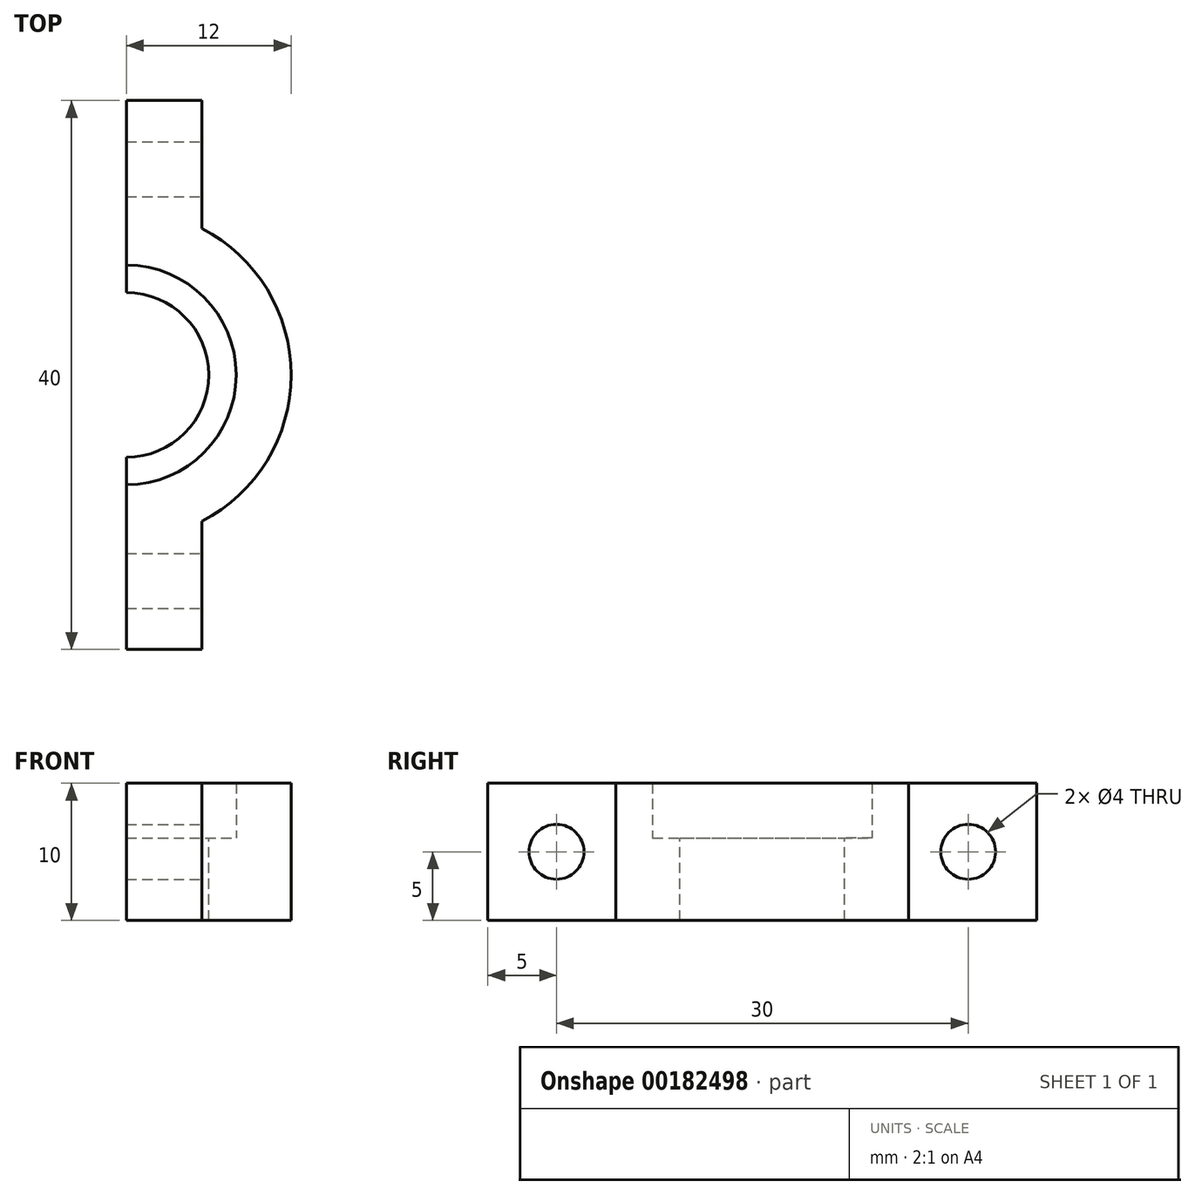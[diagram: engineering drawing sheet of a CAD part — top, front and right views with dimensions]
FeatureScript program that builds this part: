
annotation { "Feature Type Name" : "Feature", "Feature Type Description" : "" }
export const myFeature = defineFeature(function(context is Context, id is Id, definition is map)
    precondition{}
    {
        {
            var Q0;
            Q0=qCreatedBy(makeId("Top.planeOp"),FACE);
            var sketch = newSketch(context, id + "F0", { "sketchPlane" : qUnion([Q0])});
            skCircle(sketch, "E0.cCircle", {"center": v(0, 0) * mm, "radius": 46.19 * mm, "construction": true});
            skLineSegment(sketch, "E0.0", {"start": v(-80, 46.19) * mm, "end": v(80, 46.19) * mm, "construction": true});
            skLineSegment(sketch, "E0.1", {"start": v(80, 46.19) * mm, "end": v(0, -92.38) * mm, "construction": true});
            skLineSegment(sketch, "E0.2", {"start": v(0, -92.38) * mm, "end": v(-80, 46.19) * mm, "construction": true});
            skPoint(sketch, "E0.0.midPoint", {"position": v(0, 46.19) * mm});
            skLineSegment(sketch, "E1", {"start": v(40, 46.19) * mm, "end": v(60, 11.55) * mm});
            skLineSegment(sketch, "E2", {"start": v(-40, 46.19) * mm, "end": v(-60, 11.55) * mm});
            skLineSegment(sketch, "E3", {"start": v(-20, -57.74) * mm, "end": v(20, -57.74) * mm});
            skLineSegment(sketch, "E4", {"start": v(-40, 46.19) * mm, "end": v(40, 46.19) * mm});
            skLineSegment(sketch, "E5", {"start": v(60, 11.55) * mm, "end": v(20, -57.74) * mm});
            skLineSegment(sketch, "E6", {"start": v(-20, -57.74) * mm, "end": v(-60, 11.55) * mm});
            skSolve(sketch);
        }
        {
            var Q0;
            Q0=makeQuery(id+"F0.imprint","IMPRINT",FACE,{"disambiguationData":[TD([[makeQuery(id+"F0.imprint","IMPRINT",EDGE,{"derivedFrom":sQuery(id+"F0.wireOp",EDGE,"E1")}),-1.0]])]});
            extrude(context, id + "F1", {"entities" : qUnion([Q0]), "depth" : 10 * mm});
        }
        {
            var Q0;
            Q0=makeQuery(id+"F1.opExtrude","CAP_FACE",FACE,{"disambiguationData":[OSD([sQuery(id+"F0.wireOp",EDGE,"E1"),sQuery(id+"F0.wireOp",EDGE,"E2"),sQuery(id+"F0.wireOp",EDGE,"E3"),sQuery(id+"F0.wireOp",EDGE,"E4"),sQuery(id+"F0.wireOp",EDGE,"E5"),sQuery(id+"F0.wireOp",EDGE,"E6")])],"isStart":false});
            var sketch = newSketch(context, id + "F2", { "sketchPlane" : qUnion([Q0])});
            skLineSegment(sketch, "E7.0", {"start": v(-48.45, 21.55) * mm, "end": v(-5.57, -52.74) * mm});
            skLineSegment(sketch, "E7.1", {"start": v(5.57, -52.74) * mm, "end": v(48.45, 21.55) * mm});
            skLineSegment(sketch, "E7.2", {"start": v(48.45, 21.55) * mm, "end": v(42.89, 31.19) * mm});
            skLineSegment(sketch, "E7.3", {"start": v(-5.57, -52.74) * mm, "end": v(5.57, -52.74) * mm});
            skLineSegment(sketch, "E7.4", {"start": v(42.89, 31.19) * mm, "end": v(-42.89, 31.19) * mm});
            skLineSegment(sketch, "E7.5", {"start": v(-42.89, 31.19) * mm, "end": v(-48.45, 21.55) * mm});
            skSolve(sketch);
        }
        {
            var Q0;
            Q0=makeQuery(id+"F2.imprint","IMPRINT",FACE,{"disambiguationData":[TD([[makeQuery(id+"F2.imprint","IMPRINT",EDGE,{"derivedFrom":sQuery(id+"F2.wireOp",EDGE,"E7.0")}),1.0]])]});
            extrude(context, id + "F3", {"entities" : qUnion([Q0]), "operationType" : NewBodyOperationType.REMOVE, "oppositeDirection" : true, "depth" : 4 * mm});
        }
        {
            var Q0;
            Q0=makeQuery(id+"F3.boolean.opBoolean","COPY",FACE,{"derivedFrom":makeQuery(id+"F3.opExtrude","CAP_FACE",FACE,{"disambiguationData":[OSD([sQuery(id+"F2.wireOp",EDGE,"E7.0"),sQuery(id+"F2.wireOp",EDGE,"E7.1"),sQuery(id+"F2.wireOp",EDGE,"E7.2"),sQuery(id+"F2.wireOp",EDGE,"E7.3"),sQuery(id+"F2.wireOp",EDGE,"E7.4"),sQuery(id+"F2.wireOp",EDGE,"E7.5")])],"isStart":false})});
            var sketch = newSketch(context, id + "F4", { "sketchPlane" : qUnion([Q0])});
            skCircle(sketch, "E8", {"center": v(0, 0) * mm, "radius": 6 * mm});
            skLineSegment(sketch, "E9", {"start": v(0, 31.19) * mm, "end": v(0, 6) * mm});
            skLineSegment(sketch, "E10", {"start": v(0, -52.74) * mm, "end": v(0, -6) * mm});
            skLineSegment(sketch, "E11", {"start": v(5.5, 31.19) * mm, "end": v(5.5, -52.74) * mm});
            skLineSegment(sketch, "E12", {"start": v(0, 20) * mm, "end": v(5.5, 20) * mm});
            skLineSegment(sketch, "E13", {"start": v(0, -20) * mm, "end": v(5.5, -20) * mm});
            skLineSegment(sketch, "E14.0", {"start": v(-5.5, 31.19) * mm, "end": v(-5.5, -52.74) * mm});
            skCircle(sketch, "E15", {"center": v(0, 0) * mm, "radius": 8 * mm});
            skCircle(sketch, "E16", {"center": v(0, 0) * mm, "radius": 12 * mm});
            skLineSegment(sketch, "E17", {"start": v(-11.35, -42.72) * mm, "end": v(11.35, -42.72) * mm});
            skLineSegment(sketch, "E18", {"start": v(0, 20) * mm, "end": v(-5.5, 20) * mm});
            skLineSegment(sketch, "E19", {"start": v(0, -20) * mm, "end": v(-5.5, -20) * mm});
            skSolve(sketch);
        }
        {
            var Q0;
            {var subQ10=makeQuery(id+"F3.boolean.opBoolean","COPY",EDGE,{"derivedFrom":makeQuery(id+"F3.opExtrude","CAP_EDGE",EDGE,{"disambiguationData":[OSD([sQuery(id+"F2.wireOp",EDGE,"E7.5")])],"isStart":false})});Q0=makeQuery(id+"F4.imprint","IMPRINT",FACE,{"disambiguationData":[TD([[makeQuery(id+"F4.imprint","IMPRINT",EDGE,{"derivedFrom":subQ10}),1.0]])]});}
            var Q1;
            {var subQ3=sQuery(id+"F4.wireOp",EDGE,"E12");Q1=makeQuery(id+"F4.imprint","IMPRINT",FACE,{"disambiguationData":[TD([[makeQuery(id+"F4.imprint","IMPRINT",EDGE,{"derivedFrom":subQ3}),1.0]])]});}
            var Q2;
            {var subQ3=sQuery(id+"F4.wireOp",EDGE,"E18");Q2=makeQuery(id+"F4.imprint","IMPRINT",FACE,{"disambiguationData":[TD([[makeQuery(id+"F4.imprint","IMPRINT",EDGE,{"derivedFrom":subQ3}),-1.0]])]});}
            var Q3;
            {var subQ0=sQuery(id+"F4.wireOp",EDGE,"E18");Q3=makeQuery(id+"F4.imprint","IMPRINT",FACE,{"disambiguationData":[TD([[makeQuery(id+"F4.imprint","IMPRINT",EDGE,{"derivedFrom":subQ0}),1.0]])]});}
            var Q4;
            {var subQ0=sQuery(id+"F4.wireOp",EDGE,"E16");var subQ1=sQuery(id+"F4.wireOp",EDGE,"E9");var subQ2=makeQuery(id+"F4.imprint","INTERSECT",VERTEX,{"derivedFrom":[subQ1,subQ0]});Q4=makeQuery(id+"F4.imprint","IMPRINT",FACE,{"disambiguationData":[TD([[makeQuery(id+"F4.imprint","IMPRINT",EDGE,{"disambiguationData":[TD([[subQ2,-1.0]])],"derivedFrom":subQ1}),-1.0]])]});}
            var Q5;
            {var subQ0=sQuery(id+"F4.wireOp",EDGE,"E9");var subQ1=sQuery(id+"F4.wireOp",EDGE,"E8");var subQ2=makeQuery(id+"F4.imprint","INTERSECT",VERTEX,{"derivedFrom":[subQ1,subQ0]});Q5=makeQuery(id+"F4.imprint","IMPRINT",FACE,{"disambiguationData":[TD([[makeQuery(id+"F4.imprint","IMPRINT",EDGE,{"disambiguationData":[TD([[subQ2,-1.0]])],"derivedFrom":subQ1}),-1.0]])]});}
            var Q6;
            {var subQ0=sQuery(id+"F4.wireOp",EDGE,"E8");var subQ4=makeQuery(id+"F4.imprint","INTERSECT",VERTEX,{"derivedFrom":[subQ0,sQuery(id+"F4.wireOp",EDGE,"E9")]});Q6=makeQuery(id+"F4.imprint","IMPRINT",FACE,{"disambiguationData":[TD([[makeQuery(id+"F4.imprint","IMPRINT",EDGE,{"disambiguationData":[TD([[subQ4,1.0]])],"derivedFrom":subQ0}),1.0]])]});}
            var Q7;
            {var subQ0=sQuery(id+"F4.wireOp",EDGE,"E14.0");var subQ1=sQuery(id+"F4.wireOp",EDGE,"E8");var subQ2=makeQuery(id+"F4.imprint","INTERSECT",VERTEX,{"disambiguationData":[OD(0.0)],"derivedFrom":[subQ1,subQ0]});Q7=makeQuery(id+"F4.imprint","IMPRINT",FACE,{"disambiguationData":[TD([[makeQuery(id+"F4.imprint","IMPRINT",EDGE,{"disambiguationData":[TD([[subQ2,-1.0]])],"derivedFrom":subQ1}),-1.0]])]});}
            var Q8;
            {var subQ0=sQuery(id+"F4.wireOp",EDGE,"E16");var subQ1=sQuery(id+"F4.wireOp",EDGE,"E14.0");var subQ2=makeQuery(id+"F4.imprint","INTERSECT",VERTEX,{"disambiguationData":[OD(0.0)],"derivedFrom":[subQ1,subQ0]});Q8=makeQuery(id+"F4.imprint","IMPRINT",FACE,{"disambiguationData":[TD([[makeQuery(id+"F4.imprint","IMPRINT",EDGE,{"disambiguationData":[TD([[subQ2,-1.0]])],"derivedFrom":subQ1}),-1.0]])]});}
            var Q9;
            {var subQ0=sQuery(id+"F4.wireOp",EDGE,"E14.0");var subQ1=sQuery(id+"F4.wireOp",EDGE,"E8");var subQ2=makeQuery(id+"F4.imprint","INTERSECT",VERTEX,{"disambiguationData":[OD(0.0)],"derivedFrom":[subQ1,subQ0]});Q9=makeQuery(id+"F4.imprint","IMPRINT",FACE,{"disambiguationData":[TD([[makeQuery(id+"F4.imprint","IMPRINT",EDGE,{"disambiguationData":[TD([[subQ2,-1.0]])],"derivedFrom":subQ1}),1.0]])]});}
            var Q10;
            {var subQ0=sQuery(id+"F4.wireOp",EDGE,"E10");var subQ1=sQuery(id+"F4.wireOp",EDGE,"E8");var subQ2=makeQuery(id+"F4.imprint","INTERSECT",VERTEX,{"derivedFrom":[subQ1,subQ0]});Q10=makeQuery(id+"F4.imprint","IMPRINT",FACE,{"disambiguationData":[TD([[makeQuery(id+"F4.imprint","IMPRINT",EDGE,{"disambiguationData":[TD([[subQ2,1.0]])],"derivedFrom":subQ1}),-1.0]])]});}
            var Q11;
            {var subQ0=sQuery(id+"F4.wireOp",EDGE,"E16");var subQ1=sQuery(id+"F4.wireOp",EDGE,"E10");var subQ2=makeQuery(id+"F4.imprint","INTERSECT",VERTEX,{"derivedFrom":[subQ1,subQ0]});Q11=makeQuery(id+"F4.imprint","IMPRINT",FACE,{"disambiguationData":[TD([[makeQuery(id+"F4.imprint","IMPRINT",EDGE,{"disambiguationData":[TD([[subQ2,-1.0]])],"derivedFrom":subQ1}),1.0]])]});}
            var Q12;
            {var subQ0=sQuery(id+"F4.wireOp",EDGE,"E19");Q12=makeQuery(id+"F4.imprint","IMPRINT",FACE,{"disambiguationData":[TD([[makeQuery(id+"F4.imprint","IMPRINT",EDGE,{"derivedFrom":subQ0}),-1.0]])]});}
            var Q13;
            {var subQ0=sQuery(id+"F4.wireOp",EDGE,"E19");Q13=makeQuery(id+"F4.imprint","IMPRINT",FACE,{"disambiguationData":[TD([[makeQuery(id+"F4.imprint","IMPRINT",EDGE,{"derivedFrom":subQ0}),1.0]])]});}
            var Q14;
            {var subQ0=sQuery(id+"F4.wireOp",EDGE,"E13");Q14=makeQuery(id+"F4.imprint","IMPRINT",FACE,{"disambiguationData":[TD([[makeQuery(id+"F4.imprint","IMPRINT",EDGE,{"derivedFrom":subQ0}),-1.0]])]});}
            var Q15;
            {var subQ9=makeQuery(id+"F3.boolean.opBoolean","COPY",EDGE,{"derivedFrom":makeQuery(id+"F3.opExtrude","CAP_EDGE",EDGE,{"disambiguationData":[OSD([sQuery(id+"F2.wireOp",EDGE,"E7.2")])],"isStart":false})});Q15=makeQuery(id+"F4.imprint","IMPRINT",FACE,{"disambiguationData":[TD([[makeQuery(id+"F4.imprint","IMPRINT",EDGE,{"derivedFrom":subQ9}),1.0]])]});}
            var Q16;
            {var subQ0=sQuery(id+"F4.wireOp",EDGE,"E11");var subQ1=makeQuery(id+"F3.boolean.opBoolean","COPY",EDGE,{"derivedFrom":makeQuery(id+"F3.opExtrude","CAP_EDGE",EDGE,{"disambiguationData":[OSD([sQuery(id+"F2.wireOp",EDGE,"E7.3")])],"isStart":false})});var subQ2=makeQuery(id+"F4.imprint","INTERSECT",VERTEX,{"derivedFrom":[subQ1,subQ0]});Q16=makeQuery(id+"F4.imprint","IMPRINT",FACE,{"disambiguationData":[TD([[makeQuery(id+"F4.imprint","IMPRINT",EDGE,{"disambiguationData":[TD([[subQ2,1.0]])],"derivedFrom":subQ0}),1.0]])]});}
            var Q17;
            {var subQ0=sQuery(id+"F4.wireOp",EDGE,"E10");var subQ1=makeQuery(id+"F3.boolean.opBoolean","COPY",EDGE,{"derivedFrom":makeQuery(id+"F3.opExtrude","CAP_EDGE",EDGE,{"disambiguationData":[OSD([sQuery(id+"F2.wireOp",EDGE,"E7.3")])],"isStart":false})});var subQ2=makeQuery(id+"F4.imprint","INTERSECT",VERTEX,{"derivedFrom":[subQ1,subQ0]});Q17=makeQuery(id+"F4.imprint","IMPRINT",FACE,{"disambiguationData":[TD([[makeQuery(id+"F4.imprint","IMPRINT",EDGE,{"disambiguationData":[TD([[subQ2,-1.0]])],"derivedFrom":subQ0}),-1.0]])]});}
            var Q18;
            {var subQ0=sQuery(id+"F4.wireOp",EDGE,"E10");var subQ1=makeQuery(id+"F3.boolean.opBoolean","COPY",EDGE,{"derivedFrom":makeQuery(id+"F3.opExtrude","CAP_EDGE",EDGE,{"disambiguationData":[OSD([sQuery(id+"F2.wireOp",EDGE,"E7.3")])],"isStart":false})});var subQ2=makeQuery(id+"F4.imprint","INTERSECT",VERTEX,{"derivedFrom":[subQ1,subQ0]});Q18=makeQuery(id+"F4.imprint","IMPRINT",FACE,{"disambiguationData":[TD([[makeQuery(id+"F4.imprint","IMPRINT",EDGE,{"disambiguationData":[TD([[subQ2,-1.0]])],"derivedFrom":subQ0}),1.0]])]});}
            var Q19;
            {var subQ0=sQuery(id+"F4.wireOp",EDGE,"E14.0");var subQ1=makeQuery(id+"F3.boolean.opBoolean","COPY",EDGE,{"derivedFrom":makeQuery(id+"F3.opExtrude","CAP_EDGE",EDGE,{"disambiguationData":[OSD([sQuery(id+"F2.wireOp",EDGE,"E7.3")])],"isStart":false})});var subQ2=makeQuery(id+"F4.imprint","INTERSECT",VERTEX,{"derivedFrom":[subQ1,subQ0]});Q19=makeQuery(id+"F4.imprint","IMPRINT",FACE,{"disambiguationData":[TD([[makeQuery(id+"F4.imprint","IMPRINT",EDGE,{"disambiguationData":[TD([[subQ2,1.0]])],"derivedFrom":subQ0}),-1.0]])]});}
            var Q20;
            Q20=makeQuery(id+"F1.opExtrude","CAP_FACE",FACE,{"disambiguationData":[OSD([sQuery(id+"F0.wireOp",EDGE,"E1"),sQuery(id+"F0.wireOp",EDGE,"E2"),sQuery(id+"F0.wireOp",EDGE,"E3"),sQuery(id+"F0.wireOp",EDGE,"E4"),sQuery(id+"F0.wireOp",EDGE,"E5"),sQuery(id+"F0.wireOp",EDGE,"E6")])],"isStart":false});
            var Q21;
            {var subQ0=sQuery(id+"F4.wireOp",EDGE,"E11");var subQ1=sQuery(id+"F4.wireOp",EDGE,"E8");var subQ2=makeQuery(id+"F4.imprint","INTERSECT",VERTEX,{"disambiguationData":[OD(0.0)],"derivedFrom":[subQ1,subQ0]});Q21=makeQuery(id+"F4.imprint","IMPRINT",FACE,{"disambiguationData":[TD([[makeQuery(id+"F4.imprint","IMPRINT",EDGE,{"disambiguationData":[TD([[subQ2,1.0]])],"derivedFrom":subQ1}),1.0]])]});}
            extrude(context, id + "F5", {"entities" : qUnion([Q0, Q1, Q2, Q3, Q4, Q5, Q6, Q7, Q8, Q9, Q10, Q11, Q12, Q13, Q14, Q15, Q16, Q17, Q18, Q19, Q20, Q21]), "operationType" : NewBodyOperationType.REMOVE, "oppositeDirection" : true, "depth" : 25 * mm});
        }
        {
            var Q0;
            {var subQ0=sQuery(id+"F4.wireOp",EDGE,"E12");Q0=makeQuery(id+"F4.imprint","IMPRINT",FACE,{"disambiguationData":[TD([[makeQuery(id+"F4.imprint","IMPRINT",EDGE,{"derivedFrom":subQ0}),-1.0]])]});}
            var Q1;
            {var subQ0=sQuery(id+"F4.wireOp",EDGE,"E16");var subQ1=sQuery(id+"F4.wireOp",EDGE,"E9");var subQ2=makeQuery(id+"F4.imprint","INTERSECT",VERTEX,{"derivedFrom":[subQ1,subQ0]});Q1=makeQuery(id+"F4.imprint","IMPRINT",FACE,{"disambiguationData":[TD([[makeQuery(id+"F4.imprint","IMPRINT",EDGE,{"disambiguationData":[TD([[subQ2,-1.0]])],"derivedFrom":subQ1}),1.0]])]});}
            var Q2;
            {var subQ0=sQuery(id+"F4.wireOp",EDGE,"E16");var subQ1=sQuery(id+"F4.wireOp",EDGE,"E11");var subQ2=makeQuery(id+"F4.imprint","INTERSECT",VERTEX,{"disambiguationData":[OD(0.0)],"derivedFrom":[subQ1,subQ0]});Q2=makeQuery(id+"F4.imprint","IMPRINT",FACE,{"disambiguationData":[TD([[makeQuery(id+"F4.imprint","IMPRINT",EDGE,{"disambiguationData":[TD([[subQ2,-1.0]])],"derivedFrom":subQ1}),1.0]])]});}
            var Q3;
            {var subQ0=sQuery(id+"F4.wireOp",EDGE,"E16");var subQ1=sQuery(id+"F4.wireOp",EDGE,"E10");var subQ2=makeQuery(id+"F4.imprint","INTERSECT",VERTEX,{"derivedFrom":[subQ1,subQ0]});Q3=makeQuery(id+"F4.imprint","IMPRINT",FACE,{"disambiguationData":[TD([[makeQuery(id+"F4.imprint","IMPRINT",EDGE,{"disambiguationData":[TD([[subQ2,-1.0]])],"derivedFrom":subQ1}),-1.0]])]});}
            var Q4;
            {var subQ0=sQuery(id+"F4.wireOp",EDGE,"E13");Q4=makeQuery(id+"F4.imprint","IMPRINT",FACE,{"disambiguationData":[TD([[makeQuery(id+"F4.imprint","IMPRINT",EDGE,{"derivedFrom":subQ0}),1.0]])]});}
            extrude(context, id + "F6", {"entities" : qUnion([Q0, Q1, Q2, Q3, Q4]), "operationType" : NewBodyOperationType.ADD, "depth" : 4 * mm});
        }
        {
            var Q0;
            {var subQ0=sQuery(id+"F4.wireOp",EDGE,"E10");Q0=makeQuery(id+"F6.boolean.opBoolean","MERGE",FACE,{"derivedFrom":[makeQuery(id+"F5.boolean.opBoolean","COPY",FACE,{"derivedFrom":makeQuery(id+"F5.opExtrude","SWEPT_FACE",FACE,{"disambiguationData":[OSD([subQ0])]})}),makeQuery(id+"F6.opExtrude","SWEPT_FACE",FACE,{"disambiguationData":[OSD([subQ0])]})]});}
            var sketch = newSketch(context, id + "F7", { "sketchPlane" : qUnion([Q0])});
            skLineSegment(sketch, "E20", {"start": v(15, 5) * mm, "end": v(-15, 5) * mm, "construction": true});
            skSolve(sketch);
        }
        {
            var Q0;
            Q0=sQuery(id+"F7.wireOp",VERTEX,"E20.start");
            var Q1;
            Q1=sQuery(id+"F7.wireOp",VERTEX,"E20.end");
            var Q2;
            Q2=sQuery(id+"F1Wl1Qy0NJhi3PS_1.wireOp",VERTEX,"94f60bea-3120-4d41-b304-0a98c06796c9");
            var Q3;
            Q3=sQuery(id+"FXlP9DcXxy9Skzp_1.wireOp",VERTEX,"aa3b5012-087b-4bf7-bd4c-e3736290773a");
            var Q4;
            Q4=sQuery(id+"FqLlLn9KF9hdrij_1.wireOp",VERTEX,"28370442-b81d-43c0-b6ec-cbcaf4834eb6");
            var Q5;
            Q5=makeQuery(id+"F1.opExtrude","SWEPT_BODY",BODY,{"disambiguationData":[OSD([sQuery(id+"F0.wireOp",EDGE,"E1"),sQuery(id+"F0.wireOp",EDGE,"E2"),sQuery(id+"F0.wireOp",EDGE,"E3"),sQuery(id+"F0.wireOp",EDGE,"E4"),sQuery(id+"F0.wireOp",EDGE,"E5"),sQuery(id+"F0.wireOp",EDGE,"E6")])]});
            hole(context, id + "F8", {"style" : HoleStyle.SIMPLE, "endStyle" : HoleEndStyle.BLIND, "holeDiameter" : 4 * mm, "holeDepth" : 9 * mm, "locations" : qUnion([Q0, Q1, Q2, Q3, Q4]), "scope" : qUnion([Q5])});
        }
    });
